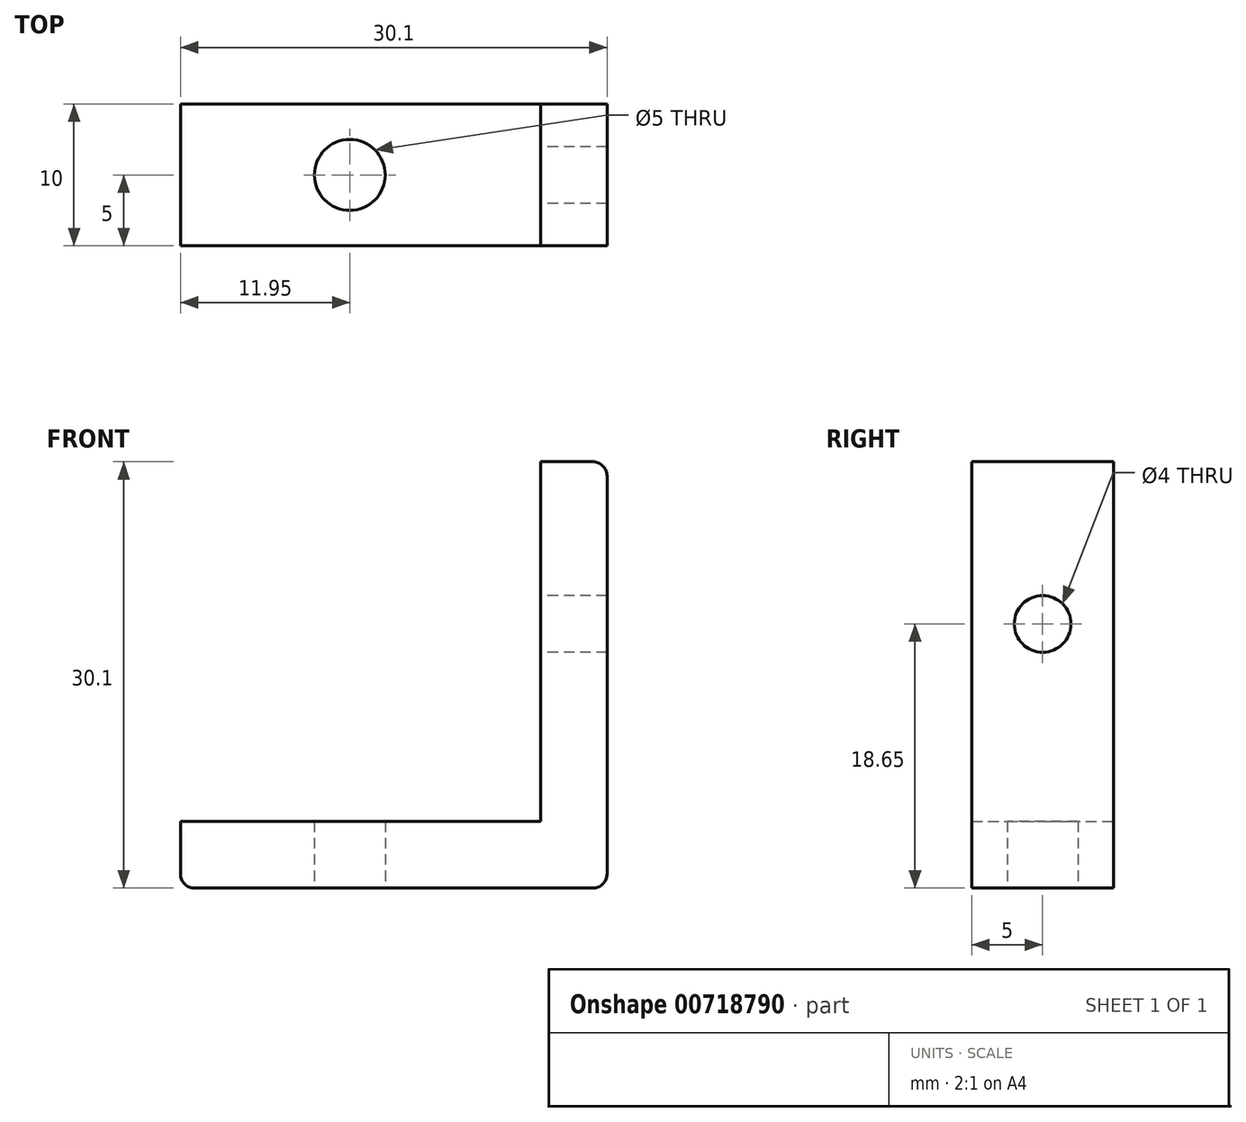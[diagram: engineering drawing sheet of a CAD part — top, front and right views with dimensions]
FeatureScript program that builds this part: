
annotation { "Feature Type Name" : "Feature", "Feature Type Description" : "" }
export const myFeature = defineFeature(function(context is Context, id is Id, definition is map)
    precondition{}
    {
        {
            var Q0;
            Q0=qCreatedBy(makeId("Top.planeOp"),FACE);
            var sketch = newSketch(context, id + "F0", { "sketchPlane" : qUnion([Q0])});
            skLineSegment(sketch, "E0.bottom", {"start": v(12.7, -5) * mm, "end": v(-12.7, -5) * mm});
            skLineSegment(sketch, "E0.top", {"start": v(12.7, 5) * mm, "end": v(-12.7, 5) * mm});
            skLineSegment(sketch, "E0.left", {"start": v(12.7, -5) * mm, "end": v(12.7, 5) * mm});
            skLineSegment(sketch, "E0.right", {"start": v(-12.7, -5) * mm, "end": v(-12.7, 5) * mm});
            skPoint(sketch, "E0.middle", {"position": v(0, 0) * mm});
            skCircle(sketch, "E1", {"center": v(-0.75, 0) * mm, "radius": 2.5 * mm});
            skSolve(sketch);
        }
        {
            var Q0;
            Q0=makeQuery(id+"F0.imprint","IMPRINT",FACE,{"disambiguationData":[TD([[makeQuery(id+"F0.imprint","IMPRINT",EDGE,{"derivedFrom":sQuery(id+"F0.wireOp",EDGE,"E0.bottom")}),-1.0]])]});
            extrude(context, id + "F1", {"entities" : qUnion([Q0]), "depth" : 4.7 * mm, "offsetDistance" : 25 * mm});
        }
        {
            var Q0;
            Q0=makeQuery(id+"F1.opExtrude","SWEPT_FACE",FACE,{"disambiguationData":[OSD([sQuery(id+"F0.wireOp",EDGE,"E0.left")])]});
            var sketch = newSketch(context, id + "F2", { "sketchPlane" : qUnion([Q0])});
            skLineSegment(sketch, "E2.bottom", {"start": v(5, 0) * mm, "end": v(-5, 0) * mm});
            skLineSegment(sketch, "E2.top", {"start": v(5, 30.1) * mm, "end": v(-5, 30.1) * mm});
            skLineSegment(sketch, "E2.left", {"start": v(5, 0) * mm, "end": v(5, 30.1) * mm});
            skLineSegment(sketch, "E2.right", {"start": v(-5, 0) * mm, "end": v(-5, 30.1) * mm});
            skCircle(sketch, "E3", {"center": v(0, 18.65) * mm, "radius": 2 * mm});
            skSolve(sketch);
        }
        {
            var Q0;
            Q0 = qSketchRegion(id + "F2", true);
            extrude(context, id + "F3", {"entities" : qUnion([Q0]), "operationType" : NewBodyOperationType.ADD, "depth" : 4.7 * mm, "offsetDistance" : 25 * mm});
        }
        {
            var Q0;
            Q0=makeQuery(id+"F3.opExtrude","CAP_EDGE",EDGE,{"disambiguationData":[OSD([sQuery(id+"F2.wireOp",EDGE,"E2.top")])],"isStart":false});
            var Q1;
            Q1=makeQuery(id+"F3.opExtrude","CAP_EDGE",EDGE,{"disambiguationData":[OSD([sQuery(id+"F2.wireOp",EDGE,"E2.bottom")])],"isStart":false});
            var Q2;
            Q2=makeQuery(id+"F1.opExtrude","CAP_EDGE",EDGE,{"disambiguationData":[OSD([sQuery(id+"F0.wireOp",EDGE,"E0.right")])],"isStart":true});
            fillet(context, id + "F4", {"entities" : qUnion([Q0, Q1, Q2]), "radius" : 1 * mm, "tangentPropagation" : true, "allowEdgeOverflow" : false});
        }
    });
